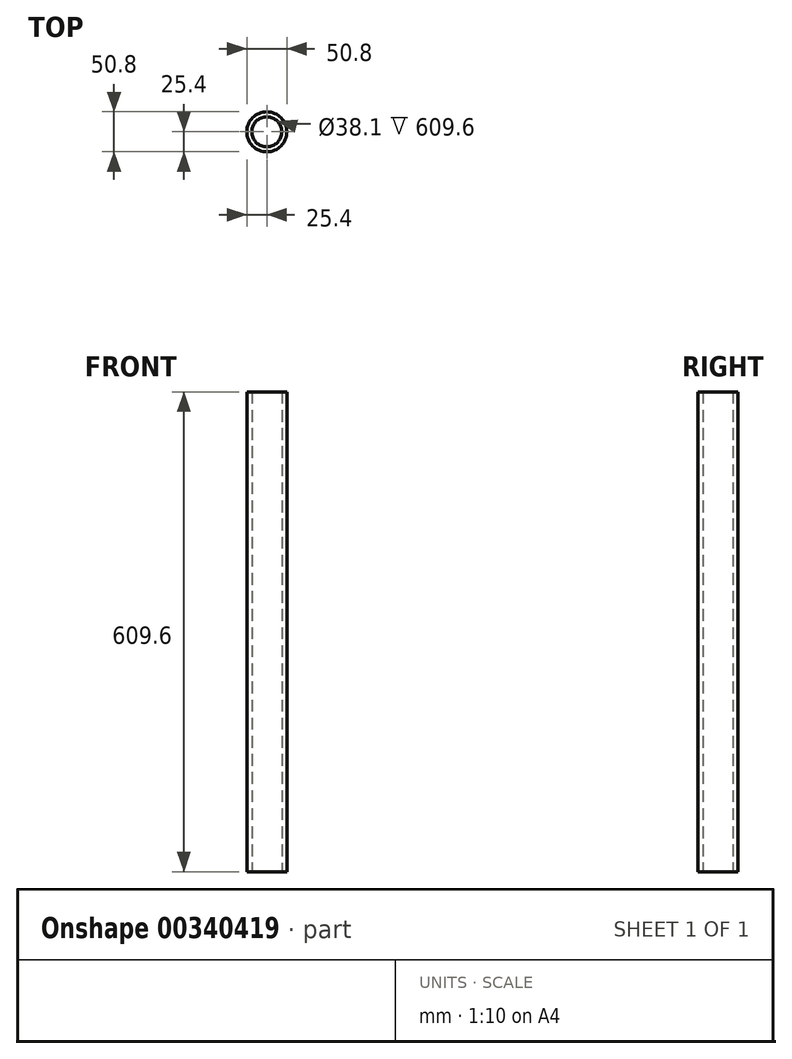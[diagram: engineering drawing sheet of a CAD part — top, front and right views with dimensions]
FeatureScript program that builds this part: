
annotation { "Feature Type Name" : "Feature", "Feature Type Description" : "" }
export const myFeature = defineFeature(function(context is Context, id is Id, definition is map)
    precondition{}
    {
        {
            var Q0;
            Q0=qCreatedBy(makeId("Top.planeOp"),FACE);
            var sketch = newSketch(context, id + "F0", { "sketchPlane" : qUnion([Q0])});
            skCircle(sketch, "E0", {"center": v(0, 0) * mm, "radius": 25.4 * mm});
            skCircle(sketch, "E1", {"center": v(0, 0) * mm, "radius": 19.05 * mm});
            skSolve(sketch);
        }
        {
            var Q0;
            Q0=makeQuery(id+"F0.imprint","IMPRINT",FACE,{"disambiguationData":[TD([[makeQuery(id+"F0.imprint","IMPRINT",EDGE,{"derivedFrom":sQuery(id+"F0.wireOp",EDGE,"E0")}),1.0]])]});
            extrude(context, id + "F1", {"entities" : qUnion([Q0]), "endBound" : BoundingType.SYMMETRIC, "depth" : 609.6 * mm});
        }
    });
